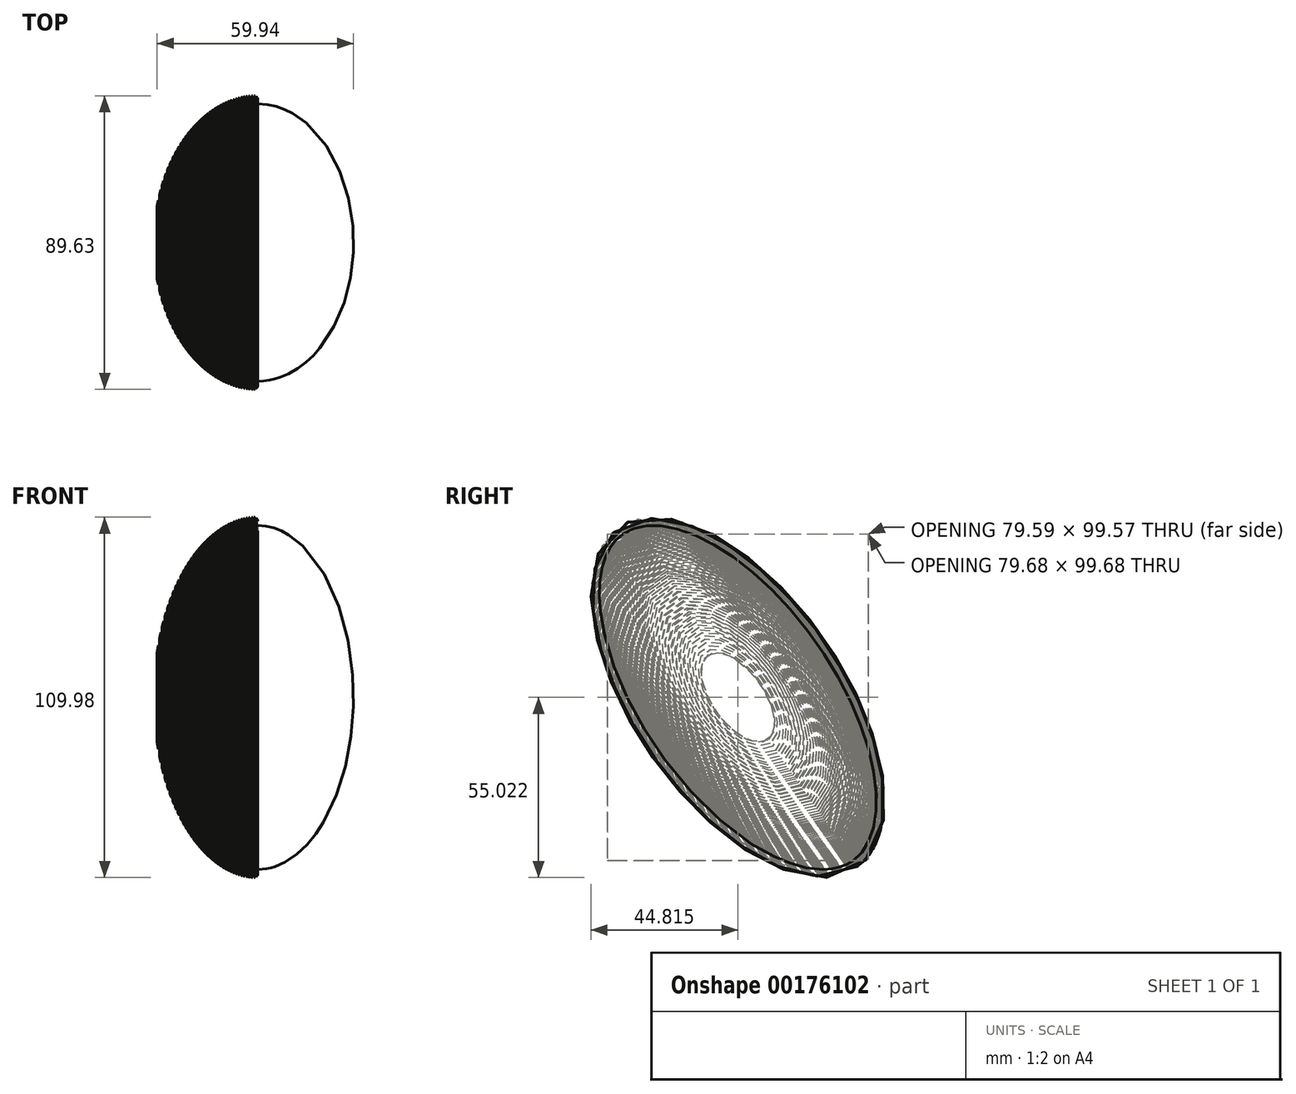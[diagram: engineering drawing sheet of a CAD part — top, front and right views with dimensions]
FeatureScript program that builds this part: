
annotation { "Feature Type Name" : "Feature", "Feature Type Description" : "" }
export const myFeature = defineFeature(function(context is Context, id is Id, definition is map)
    precondition{}
    {
        {
            var Q0;
            Q0=qCreatedBy(makeId("Right.planeOp"),FACE);
            var sketch = newSketch(context, id + "F0", { "sketchPlane" : qUnion([Q0])});
            skEllipse(sketch, "E0", {"center": v(0, 0) * mm, "majorRadius": 63.5 * mm, "minorRadius": 31.75 * mm, "majorAxis": v(-0.58, 0.82)});
            skLineSegment(sketch, "E1", {"start": v(0, 0) * mm, "end": v(-36.58, 51.9) * mm});
            skLineSegment(sketch, "E2", {"start": v(-36.58, 51.9) * mm, "end": v(36.58, -51.9) * mm});
            skSolve(sketch);
        }
        {
            var Q0;
            {var subQ0=sQuery(id+"F0.wireOp",EDGE,"E2");var subQ4=makeQuery(id+"F0.imprint","IMPRINT",VERTEX,{"derivedFrom":subQ0});Q0=makeQuery(id+"F0.imprint","IMPRINT",FACE,{"disambiguationData":[TD([[makeQuery(id+"F0.imprint","IMPRINT",EDGE,{"disambiguationData":[TD([[subQ4,1.0]])],"derivedFrom":subQ0}),-1.0]])]});}
            var Q1;
            Q1=sQuery(id+"F0.wireOp",EDGE,"E2");
            revolve(context, id + "F1", {"entities" : qUnion([Q0]), "axis" : qUnion([Q1]), "revolveType" : RevolveType.ONE_DIRECTION, "angle" : 180 * degree});
        }
        {
            var Q0;
            Q0=qCreatedBy(makeId("Right.planeOp"),FACE);
            cPlane(context, id + "F2", {"entities" : qUnion([Q0]), "cplaneType" : CPlaneType.OFFSET, "offset" : 30.73 * mm, "oppositeDirection" : true, "width" : 152.4 * mm, "height" : 152.4 * mm});
        }
        {
            var Q0;
            Q0=qCreatedBy(id+"F2.planeOp",FACE);
            var sketch = newSketch(context, id + "F3", { "sketchPlane" : qUnion([Q0])});
            skLineSegment(sketch, "E3.bottom", {"start": v(33.92, 43.72) * mm, "end": v(-38.1, 43.72) * mm});
            skLineSegment(sketch, "E3.top", {"start": v(33.92, -43.72) * mm, "end": v(-38.1, -43.72) * mm});
            skLineSegment(sketch, "E3.left", {"start": v(33.92, 43.72) * mm, "end": v(33.92, -43.72) * mm});
            skLineSegment(sketch, "E3.right", {"start": v(-38.1, 43.72) * mm, "end": v(-38.1, -43.72) * mm});
            skPoint(sketch, "E3.middle", {"position": v(-2.08, 0) * mm});
            skSolve(sketch);
        }
        {
            var Q0;
            Q0 = qSketchRegion(id + "F3", true);
            extrude(context, id + "F4", {"entities" : qUnion([Q0]), "operationType" : NewBodyOperationType.REMOVE, "oppositeDirection" : true, "depth" : 25.4 * mm});
        }
        {
            var Q0;
            Q0=makeQuery(id+"F1.opRevolve","CAP_FACE",FACE,{"disambiguationData":[OSD([sQuery(id+"F0.wireOp",EDGE,"E0"),sQuery(id+"F0.wireOp",EDGE,"E2")])],"isStart":false});
            shell(context, id + "F5", {"entities" : qUnion([Q0]), "thickness" : 2.54 * mm});
        }
        {
            var Q0;
            {var subQ0=sQuery(id+"F0.wireOp",EDGE,"E0");Q0=makeQuery(id+"F5.opShell","OFFSET_EDGE",EDGE,{"disambiguationData":[OSD([subQ0]),TDD([makeQuery(id+"F1.opRevolve","CAP_EDGE",EDGE,{"disambiguationData":[OSD([subQ0])],"isStart":true})])]});}
            var Q1;
            Q1=makeQuery(id+"F1.opRevolve","CAP_EDGE",EDGE,{"disambiguationData":[OSD([sQuery(id+"F0.wireOp",EDGE,"E0")])],"isStart":true});
            fillet(context, id + "F6", {"entities" : qUnion([Q0, Q1]), "radius" : 1.24 * mm, "tangentPropagation" : true, "allowEdgeOverflow" : false});
        }
        {
            var Q0;
            Q0=qCreatedBy(makeId("Right.planeOp"),FACE);
            cPlane(context, id + "F7", {"entities" : qUnion([Q0]), "cplaneType" : CPlaneType.OFFSET, "offset" : .4 * mm, "oppositeDirection" : true, "width" : 152.4 * mm, "height" : 152.4 * mm});
        }
        {
            var Q0;
            Q0=qCreatedBy(id+"F7.planeOp",FACE);
            cPlane(context, id + "F8", {"entities" : qUnion([Q0]), "cplaneType" : CPlaneType.OFFSET, "offset" : .8 * mm, "oppositeDirection" : true, "width" : 152.4 * mm, "height" : 152.4 * mm});
        }
        {
            var Q0;
            Q0=qCreatedBy(id+"F8.planeOp",FACE);
            cPlane(context, id + "F9", {"entities" : qUnion([Q0]), "cplaneType" : CPlaneType.OFFSET, "offset" : .8 * mm, "oppositeDirection" : true, "width" : 152.4 * mm, "height" : 152.4 * mm});
        }
        {
            var Q0;
            Q0=qCreatedBy(id+"F9.planeOp",FACE);
            cPlane(context, id + "F10", {"entities" : qUnion([Q0]), "cplaneType" : CPlaneType.OFFSET, "offset" : .8 * mm, "oppositeDirection" : true, "width" : 152.4 * mm, "height" : 152.4 * mm});
        }
        {
            var Q0;
            Q0=qCreatedBy(id+"F10.planeOp",FACE);
            cPlane(context, id + "F11", {"entities" : qUnion([Q0]), "cplaneType" : CPlaneType.OFFSET, "offset" : .8 * mm, "oppositeDirection" : true, "width" : 152.4 * mm, "height" : 152.4 * mm});
        }
        {
            var Q0;
            Q0=qCreatedBy(id+"F11.planeOp",FACE);
            cPlane(context, id + "F12", {"entities" : qUnion([Q0]), "cplaneType" : CPlaneType.OFFSET, "offset" : .8 * mm, "oppositeDirection" : true, "width" : 152.4 * mm, "height" : 152.4 * mm});
        }
        {
            var Q0;
            Q0=qCreatedBy(id+"F12.planeOp",FACE);
            cPlane(context, id + "F13", {"entities" : qUnion([Q0]), "cplaneType" : CPlaneType.OFFSET, "offset" : .8 * mm, "oppositeDirection" : true, "width" : 152.4 * mm, "height" : 152.4 * mm});
        }
        {
            var Q0;
            Q0=qCreatedBy(id+"F13.planeOp",FACE);
            cPlane(context, id + "F14", {"entities" : qUnion([Q0]), "cplaneType" : CPlaneType.OFFSET, "offset" : .8 * mm, "oppositeDirection" : true, "width" : 152.4 * mm, "height" : 152.4 * mm});
        }
        {
            var Q0;
            Q0=qCreatedBy(id+"F14.planeOp",FACE);
            cPlane(context, id + "F15", {"entities" : qUnion([Q0]), "cplaneType" : CPlaneType.OFFSET, "offset" : .8 * mm, "oppositeDirection" : true, "width" : 152.4 * mm, "height" : 152.4 * mm});
        }
        {
            var Q0;
            Q0=qCreatedBy(id+"F15.planeOp",FACE);
            cPlane(context, id + "F16", {"entities" : qUnion([Q0]), "cplaneType" : CPlaneType.OFFSET, "offset" : .8 * mm, "oppositeDirection" : true, "width" : 152.4 * mm, "height" : 152.4 * mm});
        }
        {
            var Q0;
            Q0=qCreatedBy(id+"F16.planeOp",FACE);
            cPlane(context, id + "F17", {"entities" : qUnion([Q0]), "cplaneType" : CPlaneType.OFFSET, "offset" : .8 * mm, "oppositeDirection" : true, "width" : 152.4 * mm, "height" : 152.4 * mm});
        }
        {
            var Q0;
            Q0=qCreatedBy(id+"F17.planeOp",FACE);
            cPlane(context, id + "F18", {"entities" : qUnion([Q0]), "cplaneType" : CPlaneType.OFFSET, "offset" : .8 * mm, "oppositeDirection" : true, "width" : 152.4 * mm, "height" : 152.4 * mm});
        }
        {
            var Q0;
            Q0=qCreatedBy(id+"F18.planeOp",FACE);
            cPlane(context, id + "F19", {"entities" : qUnion([Q0]), "cplaneType" : CPlaneType.OFFSET, "offset" : .8 * mm, "oppositeDirection" : true, "width" : 152.4 * mm, "height" : 152.4 * mm});
        }
        {
            var Q0;
            Q0=qCreatedBy(id+"F19.planeOp",FACE);
            cPlane(context, id + "F20", {"entities" : qUnion([Q0]), "cplaneType" : CPlaneType.OFFSET, "offset" : .8 * mm, "oppositeDirection" : true, "width" : 152.4 * mm, "height" : 152.4 * mm});
        }
        {
            var Q0;
            Q0=qCreatedBy(id+"F20.planeOp",FACE);
            cPlane(context, id + "F21", {"entities" : qUnion([Q0]), "cplaneType" : CPlaneType.OFFSET, "offset" : .8 * mm, "oppositeDirection" : true, "width" : 152.4 * mm, "height" : 152.4 * mm});
        }
        {
            var Q0;
            Q0=qCreatedBy(id+"F21.planeOp",FACE);
            cPlane(context, id + "F22", {"entities" : qUnion([Q0]), "cplaneType" : CPlaneType.OFFSET, "offset" : .8 * mm, "oppositeDirection" : true, "width" : 152.4 * mm, "height" : 152.4 * mm});
        }
        {
            var Q0;
            Q0=qCreatedBy(id+"F22.planeOp",FACE);
            cPlane(context, id + "F23", {"entities" : qUnion([Q0]), "cplaneType" : CPlaneType.OFFSET, "offset" : .8 * mm, "oppositeDirection" : true, "width" : 152.4 * mm, "height" : 152.4 * mm});
        }
        {
            var Q0;
            Q0=qCreatedBy(id+"F23.planeOp",FACE);
            cPlane(context, id + "F24", {"entities" : qUnion([Q0]), "cplaneType" : CPlaneType.OFFSET, "offset" : .8 * mm, "oppositeDirection" : true, "width" : 152.4 * mm, "height" : 152.4 * mm});
        }
        {
            var Q0;
            Q0=qCreatedBy(id+"F24.planeOp",FACE);
            cPlane(context, id + "F25", {"entities" : qUnion([Q0]), "cplaneType" : CPlaneType.OFFSET, "offset" : .8 * mm, "oppositeDirection" : true, "width" : 152.4 * mm, "height" : 152.4 * mm});
        }
        {
            var Q0;
            Q0=qCreatedBy(id+"F25.planeOp",FACE);
            cPlane(context, id + "F26", {"entities" : qUnion([Q0]), "cplaneType" : CPlaneType.OFFSET, "offset" : .8 * mm, "oppositeDirection" : true, "width" : 152.4 * mm, "height" : 152.4 * mm});
        }
        {
            var Q0;
            Q0=qCreatedBy(id+"F26.planeOp",FACE);
            cPlane(context, id + "F27", {"entities" : qUnion([Q0]), "cplaneType" : CPlaneType.OFFSET, "offset" : .8 * mm, "oppositeDirection" : true, "width" : 152.4 * mm, "height" : 152.4 * mm});
        }
        {
            var Q0;
            Q0=qCreatedBy(id+"F27.planeOp",FACE);
            cPlane(context, id + "F28", {"entities" : qUnion([Q0]), "cplaneType" : CPlaneType.OFFSET, "offset" : .8 * mm, "oppositeDirection" : true, "width" : 152.4 * mm, "height" : 152.4 * mm});
        }
        {
            var Q0;
            Q0=qCreatedBy(id+"F28.planeOp",FACE);
            cPlane(context, id + "F29", {"entities" : qUnion([Q0]), "cplaneType" : CPlaneType.OFFSET, "offset" : .8 * mm, "oppositeDirection" : true, "width" : 152.4 * mm, "height" : 152.4 * mm});
        }
        {
            var Q0;
            Q0=qCreatedBy(id+"F29.planeOp",FACE);
            cPlane(context, id + "F30", {"entities" : qUnion([Q0]), "cplaneType" : CPlaneType.OFFSET, "offset" : .8 * mm, "oppositeDirection" : true, "width" : 152.4 * mm, "height" : 152.4 * mm});
        }
        {
            var Q0;
            Q0=qCreatedBy(id+"F30.planeOp",FACE);
            cPlane(context, id + "F31", {"entities" : qUnion([Q0]), "cplaneType" : CPlaneType.OFFSET, "offset" : .8 * mm, "oppositeDirection" : true, "width" : 152.4 * mm, "height" : 152.4 * mm});
        }
        {
            var Q0;
            Q0=qCreatedBy(id+"F31.planeOp",FACE);
            cPlane(context, id + "F32", {"entities" : qUnion([Q0]), "cplaneType" : CPlaneType.OFFSET, "offset" : .8 * mm, "oppositeDirection" : true, "width" : 152.4 * mm, "height" : 152.4 * mm});
        }
        {
            var Q0;
            Q0=qCreatedBy(id+"F32.planeOp",FACE);
            cPlane(context, id + "F33", {"entities" : qUnion([Q0]), "cplaneType" : CPlaneType.OFFSET, "offset" : .8 * mm, "oppositeDirection" : true, "width" : 152.4 * mm, "height" : 152.4 * mm});
        }
        {
            var Q0;
            Q0=qCreatedBy(id+"F33.planeOp",FACE);
            cPlane(context, id + "F34", {"entities" : qUnion([Q0]), "cplaneType" : CPlaneType.OFFSET, "offset" : .8 * mm, "oppositeDirection" : true, "width" : 152.4 * mm, "height" : 152.4 * mm});
        }
        {
            var Q0;
            Q0=qCreatedBy(id+"F34.planeOp",FACE);
            cPlane(context, id + "F35", {"entities" : qUnion([Q0]), "cplaneType" : CPlaneType.OFFSET, "offset" : .8 * mm, "oppositeDirection" : true, "width" : 152.4 * mm, "height" : 152.4 * mm});
        }
        {
            var Q0;
            Q0=qCreatedBy(id+"F35.planeOp",FACE);
            cPlane(context, id + "F36", {"entities" : qUnion([Q0]), "cplaneType" : CPlaneType.OFFSET, "offset" : .8 * mm, "oppositeDirection" : true, "width" : 152.4 * mm, "height" : 152.4 * mm});
        }
        {
            var Q0;
            Q0=qCreatedBy(id+"F36.planeOp",FACE);
            cPlane(context, id + "F37", {"entities" : qUnion([Q0]), "cplaneType" : CPlaneType.OFFSET, "offset" : .8 * mm, "oppositeDirection" : true, "width" : 152.4 * mm, "height" : 152.4 * mm});
        }
        {
            var Q0;
            Q0=qCreatedBy(id+"F37.planeOp",FACE);
            cPlane(context, id + "F38", {"entities" : qUnion([Q0]), "cplaneType" : CPlaneType.OFFSET, "offset" : .8 * mm, "oppositeDirection" : true, "width" : 152.4 * mm, "height" : 152.4 * mm});
        }
        {
            var Q0;
            Q0=qCreatedBy(id+"F38.planeOp",FACE);
            cPlane(context, id + "F39", {"entities" : qUnion([Q0]), "cplaneType" : CPlaneType.OFFSET, "offset" : .8 * mm, "oppositeDirection" : true, "width" : 152.4 * mm, "height" : 152.4 * mm});
        }
        {
            var Q0;
            Q0=qCreatedBy(id+"F39.planeOp",FACE);
            cPlane(context, id + "F40", {"entities" : qUnion([Q0]), "cplaneType" : CPlaneType.OFFSET, "offset" : .8 * mm, "oppositeDirection" : true, "width" : 152.4 * mm, "height" : 152.4 * mm});
        }
        {
            var Q0;
            Q0=qCreatedBy(id+"F40.planeOp",FACE);
            cPlane(context, id + "F41", {"entities" : qUnion([Q0]), "cplaneType" : CPlaneType.OFFSET, "offset" : .8 * mm, "oppositeDirection" : true, "width" : 152.4 * mm, "height" : 152.4 * mm});
        }
        {
            var Q0;
            Q0=qCreatedBy(id+"F41.planeOp",FACE);
            cPlane(context, id + "F42", {"entities" : qUnion([Q0]), "cplaneType" : CPlaneType.OFFSET, "offset" : .8 * mm, "oppositeDirection" : true, "width" : 152.4 * mm, "height" : 152.4 * mm});
        }
        {
            var Q0;
            Q0=qCreatedBy(id+"F42.planeOp",FACE);
            cPlane(context, id + "F43", {"entities" : qUnion([Q0]), "cplaneType" : CPlaneType.OFFSET, "offset" : .8 * mm, "oppositeDirection" : true, "width" : 152.4 * mm, "height" : 152.4 * mm});
        }
        {
            var Q0;
            Q0=qCreatedBy(id+"F43.planeOp",FACE);
            cPlane(context, id + "F44", {"entities" : qUnion([Q0]), "cplaneType" : CPlaneType.OFFSET, "offset" : .8 * mm, "oppositeDirection" : true, "width" : 152.4 * mm, "height" : 152.4 * mm});
        }
        {
            var Q0;
            Q0=qCreatedBy(id+"F7.planeOp",FACE);
            var sketch = newSketch(context, id + "F45", { "sketchPlane" : qUnion([Q0])});
            skLineSegment(sketch, "E4.bottom", {"start": v(-49.25, 57.03) * mm, "end": v(49.25, 57.03) * mm});
            skLineSegment(sketch, "E4.top", {"start": v(-49.25, -57.03) * mm, "end": v(49.25, -57.03) * mm});
            skLineSegment(sketch, "E4.left", {"start": v(-49.25, 57.03) * mm, "end": v(-49.25, -57.03) * mm});
            skLineSegment(sketch, "E4.right", {"start": v(49.25, 57.03) * mm, "end": v(49.25, -57.03) * mm});
            skPoint(sketch, "E4.middle", {"position": v(0, 0) * mm});
            skSolve(sketch);
        }
        {
            var Q0;
            Q0 = qSketchRegion(id + "F45", true);
            extrude(context, id + "F46", {"entities" : qUnion([Q0]), "operationType" : NewBodyOperationType.REMOVE, "oppositeDirection" : true, "depth" : .4 * mm});
        }
        {
            var Q0;
            Q0=qCreatedBy(id+"F8.planeOp",FACE);
            var sketch = newSketch(context, id + "F47", { "sketchPlane" : qUnion([Q0])});
            skLineSegment(sketch, "E5.bottom", {"start": v(53.57, 63.62) * mm, "end": v(-53.57, 63.62) * mm});
            skLineSegment(sketch, "E5.top", {"start": v(53.57, -63.62) * mm, "end": v(-53.57, -63.62) * mm});
            skLineSegment(sketch, "E5.left", {"start": v(53.57, 63.62) * mm, "end": v(53.57, -63.62) * mm});
            skLineSegment(sketch, "E5.right", {"start": v(-53.57, 63.62) * mm, "end": v(-53.57, -63.62) * mm});
            skPoint(sketch, "E5.middle", {"position": v(0, 0) * mm});
            skSolve(sketch);
        }
        {
            var Q0;
            Q0 = qSketchRegion(id + "F47", true);
            extrude(context, id + "F48", {"entities" : qUnion([Q0]), "operationType" : NewBodyOperationType.REMOVE, "oppositeDirection" : true, "depth" : .4 * mm});
        }
        {
            var Q0;
            Q0=qCreatedBy(id+"F9.planeOp",FACE);
            var sketch = newSketch(context, id + "F49", { "sketchPlane" : qUnion([Q0])});
            skLineSegment(sketch, "E6.bottom", {"start": v(-59.34, 63.85) * mm, "end": v(59.34, 63.85) * mm});
            skLineSegment(sketch, "E6.top", {"start": v(-59.34, -63.85) * mm, "end": v(59.34, -63.85) * mm});
            skLineSegment(sketch, "E6.left", {"start": v(-59.34, 63.85) * mm, "end": v(-59.34, -63.85) * mm});
            skLineSegment(sketch, "E6.right", {"start": v(59.34, 63.85) * mm, "end": v(59.34, -63.85) * mm});
            skPoint(sketch, "E6.middle", {"position": v(0, 0) * mm});
            skSolve(sketch);
        }
        {
            var Q0;
            Q0 = qSketchRegion(id + "F49", true);
            extrude(context, id + "F50", {"entities" : qUnion([Q0]), "operationType" : NewBodyOperationType.REMOVE, "oppositeDirection" : true, "depth" : .4 * mm});
        }
        {
            var Q0;
            Q0=qCreatedBy(id+"F10.planeOp",FACE);
            var sketch = newSketch(context, id + "F51", { "sketchPlane" : qUnion([Q0])});
            skLineSegment(sketch, "E7.bottom", {"start": v(-54.53, 72.46) * mm, "end": v(54.53, 72.46) * mm});
            skLineSegment(sketch, "E7.top", {"start": v(-54.53, -72.46) * mm, "end": v(54.53, -72.46) * mm});
            skLineSegment(sketch, "E7.left", {"start": v(-54.53, 72.46) * mm, "end": v(-54.53, -72.46) * mm});
            skLineSegment(sketch, "E7.right", {"start": v(54.53, 72.46) * mm, "end": v(54.53, -72.46) * mm});
            skPoint(sketch, "E7.middle", {"position": v(0, 0) * mm});
            skSolve(sketch);
        }
        {
            var Q0;
            Q0 = qSketchRegion(id + "F51", true);
            extrude(context, id + "F52", {"entities" : qUnion([Q0]), "operationType" : NewBodyOperationType.REMOVE, "oppositeDirection" : true, "depth" : .4 * mm});
        }
        {
            var Q0;
            Q0=qCreatedBy(id+"F11.planeOp",FACE);
            var sketch = newSketch(context, id + "F53", { "sketchPlane" : qUnion([Q0])});
            skLineSegment(sketch, "E8.bottom", {"start": v(-58.86, 71.77) * mm, "end": v(71.33, 71.77) * mm});
            skLineSegment(sketch, "E8.top", {"start": v(-58.86, -71.77) * mm, "end": v(71.33, -71.77) * mm});
            skLineSegment(sketch, "E8.left", {"start": v(-58.86, 71.77) * mm, "end": v(-58.86, -71.77) * mm});
            skLineSegment(sketch, "E8.right", {"start": v(71.33, 71.77) * mm, "end": v(71.33, -71.77) * mm});
            skPoint(sketch, "E8.middle", {"position": v(6.24, 0) * mm});
            skSolve(sketch);
        }
        {
            var Q0;
            Q0 = qSketchRegion(id + "F53", true);
            extrude(context, id + "F54", {"entities" : qUnion([Q0]), "operationType" : NewBodyOperationType.REMOVE, "oppositeDirection" : true, "depth" : .4 * mm});
        }
        {
            var Q0;
            Q0=qCreatedBy(id+"F12.planeOp",FACE);
            var sketch = newSketch(context, id + "F55", { "sketchPlane" : qUnion([Q0])});
            skLineSegment(sketch, "E9.bottom", {"start": v(65.58, 62.46) * mm, "end": v(-65.58, 62.46) * mm});
            skLineSegment(sketch, "E9.top", {"start": v(65.58, -62.46) * mm, "end": v(-65.58, -62.46) * mm});
            skLineSegment(sketch, "E9.left", {"start": v(65.58, 62.46) * mm, "end": v(65.58, -62.46) * mm});
            skLineSegment(sketch, "E9.right", {"start": v(-65.58, 62.46) * mm, "end": v(-65.58, -62.46) * mm});
            skPoint(sketch, "E9.middle", {"position": v(0, 0) * mm});
            skSolve(sketch);
        }
        {
            var Q0;
            Q0=qCreatedBy(id+"F13.planeOp",FACE);
            var sketch = newSketch(context, id + "F56", { "sketchPlane" : qUnion([Q0])});
            skLineSegment(sketch, "E10.bottom", {"start": v(67.66, 61.77) * mm, "end": v(-67.66, 61.77) * mm});
            skLineSegment(sketch, "E10.top", {"start": v(67.66, -61.77) * mm, "end": v(-67.66, -61.77) * mm});
            skLineSegment(sketch, "E10.left", {"start": v(67.66, 61.77) * mm, "end": v(67.66, -61.77) * mm});
            skLineSegment(sketch, "E10.right", {"start": v(-67.66, 61.77) * mm, "end": v(-67.66, -61.77) * mm});
            skPoint(sketch, "E10.middle", {"position": v(0, 0) * mm});
            skSolve(sketch);
        }
        {
            var Q0;
            Q0=qCreatedBy(id+"F14.planeOp",FACE);
            var sketch = newSketch(context, id + "F57", { "sketchPlane" : qUnion([Q0])});
            skLineSegment(sketch, "E11.bottom", {"start": v(70.2, 68.7) * mm, "end": v(-70.2, 68.7) * mm});
            skLineSegment(sketch, "E11.top", {"start": v(70.2, -68.7) * mm, "end": v(-70.2, -68.7) * mm});
            skLineSegment(sketch, "E11.left", {"start": v(70.2, 68.7) * mm, "end": v(70.2, -68.7) * mm});
            skLineSegment(sketch, "E11.right", {"start": v(-70.2, 68.7) * mm, "end": v(-70.2, -68.7) * mm});
            skPoint(sketch, "E11.middle", {"position": v(0, 0) * mm});
            skSolve(sketch);
        }
        {
            var Q0;
            Q0=qCreatedBy(id+"F15.planeOp",FACE);
            var sketch = newSketch(context, id + "F58", { "sketchPlane" : qUnion([Q0])});
            skLineSegment(sketch, "E12.bottom", {"start": v(66.27, 65) * mm, "end": v(-66.27, 65) * mm});
            skLineSegment(sketch, "E12.top", {"start": v(66.27, -65) * mm, "end": v(-66.27, -65) * mm});
            skLineSegment(sketch, "E12.left", {"start": v(66.27, 65) * mm, "end": v(66.27, -65) * mm});
            skLineSegment(sketch, "E12.right", {"start": v(-66.27, 65) * mm, "end": v(-66.27, -65) * mm});
            skPoint(sketch, "E12.middle", {"position": v(0, 0) * mm});
            skSolve(sketch);
        }
        {
            var Q0;
            Q0=qCreatedBy(id+"F16.planeOp",FACE);
            var sketch = newSketch(context, id + "F59", { "sketchPlane" : qUnion([Q0])});
            skLineSegment(sketch, "E13.bottom", {"start": v(68.35, 68) * mm, "end": v(-68.35, 68) * mm});
            skLineSegment(sketch, "E13.top", {"start": v(68.35, -68) * mm, "end": v(-68.35, -68) * mm});
            skLineSegment(sketch, "E13.left", {"start": v(68.35, 68) * mm, "end": v(68.35, -68) * mm});
            skLineSegment(sketch, "E13.right", {"start": v(-68.35, 68) * mm, "end": v(-68.35, -68) * mm});
            skPoint(sketch, "E13.middle", {"position": v(0, 0) * mm});
            skSolve(sketch);
        }
        {
            var Q0;
            Q0=qCreatedBy(id+"F17.planeOp",FACE);
            var sketch = newSketch(context, id + "F60", { "sketchPlane" : qUnion([Q0])});
            skLineSegment(sketch, "E14.bottom", {"start": v(68.35, 68.46) * mm, "end": v(-68.35, 68.46) * mm});
            skLineSegment(sketch, "E14.top", {"start": v(68.35, -68.46) * mm, "end": v(-68.35, -68.46) * mm});
            skLineSegment(sketch, "E14.left", {"start": v(68.35, 68.46) * mm, "end": v(68.35, -68.46) * mm});
            skLineSegment(sketch, "E14.right", {"start": v(-68.35, 68.46) * mm, "end": v(-68.35, -68.46) * mm});
            skPoint(sketch, "E14.middle", {"position": v(0, 0) * mm});
            skSolve(sketch);
        }
        {
            var Q0;
            Q0=qCreatedBy(id+"F18.planeOp",FACE);
            var sketch = newSketch(context, id + "F61", { "sketchPlane" : qUnion([Q0])});
            skLineSegment(sketch, "E15.bottom", {"start": v(69.27, 68.46) * mm, "end": v(-69.27, 68.46) * mm});
            skLineSegment(sketch, "E15.top", {"start": v(69.27, -68.46) * mm, "end": v(-69.27, -68.46) * mm});
            skLineSegment(sketch, "E15.left", {"start": v(69.27, 68.46) * mm, "end": v(69.27, -68.46) * mm});
            skLineSegment(sketch, "E15.right", {"start": v(-69.27, 68.46) * mm, "end": v(-69.27, -68.46) * mm});
            skPoint(sketch, "E15.middle", {"position": v(0, 0) * mm});
            skSolve(sketch);
        }
        {
            var Q0;
            Q0=qCreatedBy(id+"F19.planeOp",FACE);
            var sketch = newSketch(context, id + "F62", { "sketchPlane" : qUnion([Q0])});
            skLineSegment(sketch, "E16.bottom", {"start": v(69.73, 68) * mm, "end": v(-69.73, 68) * mm});
            skLineSegment(sketch, "E16.top", {"start": v(69.73, -68) * mm, "end": v(-69.73, -68) * mm});
            skLineSegment(sketch, "E16.left", {"start": v(69.73, 68) * mm, "end": v(69.73, -68) * mm});
            skLineSegment(sketch, "E16.right", {"start": v(-69.73, 68) * mm, "end": v(-69.73, -68) * mm});
            skPoint(sketch, "E16.middle", {"position": v(0, 0) * mm});
            skSolve(sketch);
        }
        {
            var Q0;
            Q0=qCreatedBy(id+"F20.planeOp",FACE);
            var sketch = newSketch(context, id + "F63", { "sketchPlane" : qUnion([Q0])});
            skLineSegment(sketch, "E17.bottom", {"start": v(70.89, 67.3) * mm, "end": v(-70.89, 67.3) * mm});
            skLineSegment(sketch, "E17.top", {"start": v(70.89, -67.3) * mm, "end": v(-70.89, -67.3) * mm});
            skLineSegment(sketch, "E17.left", {"start": v(70.89, 67.3) * mm, "end": v(70.89, -67.3) * mm});
            skLineSegment(sketch, "E17.right", {"start": v(-70.89, 67.3) * mm, "end": v(-70.89, -67.3) * mm});
            skPoint(sketch, "E17.middle", {"position": v(0, 0) * mm});
            skSolve(sketch);
        }
        {
            var Q0;
            Q0=qCreatedBy(id+"F21.planeOp",FACE);
            var sketch = newSketch(context, id + "F64", { "sketchPlane" : qUnion([Q0])});
            skLineSegment(sketch, "E18.bottom", {"start": v(69.97, 66.62) * mm, "end": v(-69.97, 66.62) * mm});
            skLineSegment(sketch, "E18.top", {"start": v(69.97, -66.62) * mm, "end": v(-69.97, -66.62) * mm});
            skLineSegment(sketch, "E18.left", {"start": v(69.97, 66.62) * mm, "end": v(69.97, -66.62) * mm});
            skLineSegment(sketch, "E18.right", {"start": v(-69.97, 66.62) * mm, "end": v(-69.97, -66.62) * mm});
            skPoint(sketch, "E18.middle", {"position": v(0, 0) * mm});
            skSolve(sketch);
        }
        {
            var Q0;
            Q0=qCreatedBy(id+"F22.planeOp",FACE);
            var sketch = newSketch(context, id + "F65", { "sketchPlane" : qUnion([Q0])});
            skLineSegment(sketch, "E19.bottom", {"start": v(70.2, 67.3) * mm, "end": v(-70.2, 67.3) * mm});
            skLineSegment(sketch, "E19.top", {"start": v(70.2, -67.3) * mm, "end": v(-70.2, -67.3) * mm});
            skLineSegment(sketch, "E19.left", {"start": v(70.2, 67.3) * mm, "end": v(70.2, -67.3) * mm});
            skLineSegment(sketch, "E19.right", {"start": v(-70.2, 67.3) * mm, "end": v(-70.2, -67.3) * mm});
            skPoint(sketch, "E19.middle", {"position": v(0, 0) * mm});
            skSolve(sketch);
        }
        {
            var Q0;
            Q0=qCreatedBy(id+"F23.planeOp",FACE);
            var sketch = newSketch(context, id + "F66", { "sketchPlane" : qUnion([Q0])});
            skLineSegment(sketch, "E20.bottom", {"start": v(-68.35, 66.85) * mm, "end": v(68.35, 66.85) * mm});
            skLineSegment(sketch, "E20.top", {"start": v(-68.35, -66.85) * mm, "end": v(68.35, -66.85) * mm});
            skLineSegment(sketch, "E20.left", {"start": v(-68.35, 66.85) * mm, "end": v(-68.35, -66.85) * mm});
            skLineSegment(sketch, "E20.right", {"start": v(68.35, 66.85) * mm, "end": v(68.35, -66.85) * mm});
            skPoint(sketch, "E20.middle", {"position": v(0, 0) * mm});
            skSolve(sketch);
        }
        {
            var Q0;
            Q0=qCreatedBy(id+"F24.planeOp",FACE);
            var sketch = newSketch(context, id + "F67", { "sketchPlane" : qUnion([Q0])});
            skLineSegment(sketch, "E21.bottom", {"start": v(-68.12, 65.23) * mm, "end": v(68.12, 65.23) * mm});
            skLineSegment(sketch, "E21.top", {"start": v(-68.12, -65.23) * mm, "end": v(68.12, -65.23) * mm});
            skLineSegment(sketch, "E21.left", {"start": v(-68.12, 65.23) * mm, "end": v(-68.12, -65.23) * mm});
            skLineSegment(sketch, "E21.right", {"start": v(68.12, 65.23) * mm, "end": v(68.12, -65.23) * mm});
            skPoint(sketch, "E21.middle", {"position": v(0, 0) * mm});
            skSolve(sketch);
        }
        {
            var Q0;
            Q0=qCreatedBy(id+"F25.planeOp",FACE);
            var sketch = newSketch(context, id + "F68", { "sketchPlane" : qUnion([Q0])});
            skLineSegment(sketch, "E22.bottom", {"start": v(-69.97, 67.08) * mm, "end": v(69.97, 67.08) * mm});
            skLineSegment(sketch, "E22.top", {"start": v(-69.97, -67.08) * mm, "end": v(69.97, -67.08) * mm});
            skLineSegment(sketch, "E22.left", {"start": v(-69.97, 67.08) * mm, "end": v(-69.97, -67.08) * mm});
            skLineSegment(sketch, "E22.right", {"start": v(69.97, 67.08) * mm, "end": v(69.97, -67.08) * mm});
            skPoint(sketch, "E22.middle", {"position": v(0, 0) * mm});
            skSolve(sketch);
        }
        {
            var Q0;
            Q0=qCreatedBy(id+"F26.planeOp",FACE);
            var sketch = newSketch(context, id + "F69", { "sketchPlane" : qUnion([Q0])});
            skLineSegment(sketch, "E23.bottom", {"start": v(-69.27, 66.85) * mm, "end": v(69.27, 66.85) * mm});
            skLineSegment(sketch, "E23.top", {"start": v(-69.27, -66.85) * mm, "end": v(69.27, -66.85) * mm});
            skLineSegment(sketch, "E23.left", {"start": v(-69.27, 66.85) * mm, "end": v(-69.27, -66.85) * mm});
            skLineSegment(sketch, "E23.right", {"start": v(69.27, 66.85) * mm, "end": v(69.27, -66.85) * mm});
            skPoint(sketch, "E23.middle", {"position": v(0, 0) * mm});
            skSolve(sketch);
        }
        {
            var Q0;
            Q0=qCreatedBy(id+"F27.planeOp",FACE);
            var sketch = newSketch(context, id + "F70", { "sketchPlane" : qUnion([Q0])});
            skLineSegment(sketch, "E24.bottom", {"start": v(-69.5, 66.62) * mm, "end": v(69.5, 66.62) * mm});
            skLineSegment(sketch, "E24.top", {"start": v(-69.5, -66.62) * mm, "end": v(69.5, -66.62) * mm});
            skLineSegment(sketch, "E24.left", {"start": v(-69.5, 66.62) * mm, "end": v(-69.5, -66.62) * mm});
            skLineSegment(sketch, "E24.right", {"start": v(69.5, 66.62) * mm, "end": v(69.5, -66.62) * mm});
            skPoint(sketch, "E24.middle", {"position": v(0, 0) * mm});
            skSolve(sketch);
        }
        {
            var Q0;
            Q0 = qSketchRegion(id + "F70", true);
            var Q1;
            Q1 = qSketchRegion(id + "F69", true);
            var Q2;
            Q2 = qSketchRegion(id + "F68", true);
            var Q3;
            Q3 = qSketchRegion(id + "F67", true);
            var Q4;
            Q4 = qSketchRegion(id + "F66", true);
            var Q5;
            Q5 = qSketchRegion(id + "F65", true);
            var Q6;
            Q6 = qSketchRegion(id + "F64", true);
            var Q7;
            Q7 = qSketchRegion(id + "F63", true);
            var Q8;
            Q8 = qSketchRegion(id + "F62", true);
            var Q9;
            Q9 = qSketchRegion(id + "F61", true);
            var Q10;
            Q10 = qSketchRegion(id + "F60", true);
            var Q11;
            Q11 = qSketchRegion(id + "F59", true);
            var Q12;
            Q12 = qSketchRegion(id + "F58", true);
            var Q13;
            Q13 = qSketchRegion(id + "F57", true);
            var Q14;
            Q14 = qSketchRegion(id + "F56", true);
            var Q15;
            Q15 = qSketchRegion(id + "F55", true);
            extrude(context, id + "F71", {"entities" : qUnion([Q0, Q1, Q2, Q3, Q4, Q5, Q6, Q7, Q8, Q9, Q10, Q11, Q12, Q13, Q14, Q15]), "operationType" : NewBodyOperationType.REMOVE, "oppositeDirection" : true, "depth" : .4 * mm});
        }
        {
            var Q0;
            Q0=qCreatedBy(id+"F28.planeOp",FACE);
            var sketch = newSketch(context, id + "F72", { "sketchPlane" : qUnion([Q0])});
            skLineSegment(sketch, "E25.bottom", {"start": v(-62.11, 65.46) * mm, "end": v(62.11, 65.46) * mm});
            skLineSegment(sketch, "E25.top", {"start": v(-62.11, -65.46) * mm, "end": v(62.11, -65.46) * mm});
            skLineSegment(sketch, "E25.left", {"start": v(-62.11, 65.46) * mm, "end": v(-62.11, -65.46) * mm});
            skLineSegment(sketch, "E25.right", {"start": v(62.11, 65.46) * mm, "end": v(62.11, -65.46) * mm});
            skPoint(sketch, "E25.middle", {"position": v(0, 0) * mm});
            skSolve(sketch);
        }
        {
            var Q0;
            Q0=qCreatedBy(id+"F29.planeOp",FACE);
            var sketch = newSketch(context, id + "F73", { "sketchPlane" : qUnion([Q0])});
            skLineSegment(sketch, "E26.bottom", {"start": v(-61.42, 65.23) * mm, "end": v(61.42, 65.23) * mm});
            skLineSegment(sketch, "E26.top", {"start": v(-61.42, -65.23) * mm, "end": v(61.42, -65.23) * mm});
            skLineSegment(sketch, "E26.left", {"start": v(-61.42, 65.23) * mm, "end": v(-61.42, -65.23) * mm});
            skLineSegment(sketch, "E26.right", {"start": v(61.42, 65.23) * mm, "end": v(61.42, -65.23) * mm});
            skPoint(sketch, "E26.middle", {"position": v(0, 0) * mm});
            skSolve(sketch);
        }
        {
            var Q0;
            Q0=qCreatedBy(id+"F30.planeOp",FACE);
            var sketch = newSketch(context, id + "F74", { "sketchPlane" : qUnion([Q0])});
            skLineSegment(sketch, "E27.bottom", {"start": v(-62.8, 65.23) * mm, "end": v(62.8, 65.23) * mm});
            skLineSegment(sketch, "E27.top", {"start": v(-62.8, -65.23) * mm, "end": v(62.8, -65.23) * mm});
            skLineSegment(sketch, "E27.left", {"start": v(-62.8, 65.23) * mm, "end": v(-62.8, -65.23) * mm});
            skLineSegment(sketch, "E27.right", {"start": v(62.8, 65.23) * mm, "end": v(62.8, -65.23) * mm});
            skPoint(sketch, "E27.middle", {"position": v(0, 0) * mm});
            skSolve(sketch);
        }
        {
            var Q0;
            Q0=qCreatedBy(id+"F31.planeOp",FACE);
            var sketch = newSketch(context, id + "F75", { "sketchPlane" : qUnion([Q0])});
            skLineSegment(sketch, "E28.bottom", {"start": v(-62.58, 64.54) * mm, "end": v(62.58, 64.54) * mm});
            skLineSegment(sketch, "E28.top", {"start": v(-62.58, -64.54) * mm, "end": v(62.58, -64.54) * mm});
            skLineSegment(sketch, "E28.left", {"start": v(-62.58, 64.54) * mm, "end": v(-62.58, -64.54) * mm});
            skLineSegment(sketch, "E28.right", {"start": v(62.58, 64.54) * mm, "end": v(62.58, -64.54) * mm});
            skPoint(sketch, "E28.middle", {"position": v(0, 0) * mm});
            skSolve(sketch);
        }
        {
            var Q0;
            Q0=qCreatedBy(id+"F32.planeOp",FACE);
            var sketch = newSketch(context, id + "F76", { "sketchPlane" : qUnion([Q0])});
            skLineSegment(sketch, "E29.bottom", {"start": v(-63.96, 65) * mm, "end": v(63.96, 65) * mm});
            skLineSegment(sketch, "E29.top", {"start": v(-63.96, -65) * mm, "end": v(63.96, -65) * mm});
            skLineSegment(sketch, "E29.left", {"start": v(-63.96, 65) * mm, "end": v(-63.96, -65) * mm});
            skLineSegment(sketch, "E29.right", {"start": v(63.96, 65) * mm, "end": v(63.96, -65) * mm});
            skPoint(sketch, "E29.middle", {"position": v(0, 0) * mm});
            skSolve(sketch);
        }
        {
            var Q0;
            Q0 = qSketchRegion(id + "F73", true);
            var Q1;
            Q1 = qSketchRegion(id + "F72", true);
            var Q2;
            Q2 = qSketchRegion(id + "F74", true);
            var Q3;
            Q3 = qSketchRegion(id + "F75", true);
            var Q4;
            Q4 = qSketchRegion(id + "F76", true);
            extrude(context, id + "F77", {"entities" : qUnion([Q0, Q1, Q2, Q3, Q4]), "operationType" : NewBodyOperationType.REMOVE, "oppositeDirection" : true, "depth" : .4 * mm});
        }
        {
            var Q0;
            Q0=qCreatedBy(id+"F33.planeOp",FACE);
            var sketch = newSketch(context, id + "F78", { "sketchPlane" : qUnion([Q0])});
            skLineSegment(sketch, "E30.bottom", {"start": v(67.11, 60.49) * mm, "end": v(-67.11, 60.49) * mm});
            skLineSegment(sketch, "E30.top", {"start": v(67.11, -60.49) * mm, "end": v(-67.11, -60.49) * mm});
            skLineSegment(sketch, "E30.left", {"start": v(67.11, 60.49) * mm, "end": v(67.11, -60.49) * mm});
            skLineSegment(sketch, "E30.right", {"start": v(-67.11, 60.49) * mm, "end": v(-67.11, -60.49) * mm});
            skPoint(sketch, "E30.middle", {"position": v(0, 0) * mm});
            skSolve(sketch);
        }
        {
            var Q0;
            Q0=qCreatedBy(id+"F34.planeOp",FACE);
            var sketch = newSketch(context, id + "F79", { "sketchPlane" : qUnion([Q0])});
            skLineSegment(sketch, "E31.bottom", {"start": v(66.92, 59.71) * mm, "end": v(-66.92, 59.71) * mm});
            skLineSegment(sketch, "E31.top", {"start": v(66.92, -59.71) * mm, "end": v(-66.92, -59.71) * mm});
            skLineSegment(sketch, "E31.left", {"start": v(66.92, 59.71) * mm, "end": v(66.92, -59.71) * mm});
            skLineSegment(sketch, "E31.right", {"start": v(-66.92, 59.71) * mm, "end": v(-66.92, -59.71) * mm});
            skPoint(sketch, "E31.middle", {"position": v(0, 0) * mm});
            skSolve(sketch);
        }
        {
            var Q0;
            Q0=qCreatedBy(id+"F35.planeOp",FACE);
            var sketch = newSketch(context, id + "F80", { "sketchPlane" : qUnion([Q0])});
            skLineSegment(sketch, "E32.bottom", {"start": v(66.72, 59.32) * mm, "end": v(-66.72, 59.32) * mm});
            skLineSegment(sketch, "E32.top", {"start": v(66.72, -59.32) * mm, "end": v(-66.72, -59.32) * mm});
            skLineSegment(sketch, "E32.left", {"start": v(66.72, 59.32) * mm, "end": v(66.72, -59.32) * mm});
            skLineSegment(sketch, "E32.right", {"start": v(-66.72, 59.32) * mm, "end": v(-66.72, -59.32) * mm});
            skPoint(sketch, "E32.middle", {"position": v(0, 0) * mm});
            skSolve(sketch);
        }
        {
            var Q0;
            Q0=qCreatedBy(id+"F36.planeOp",FACE);
            var sketch = newSketch(context, id + "F81", { "sketchPlane" : qUnion([Q0])});
            skLineSegment(sketch, "E33.bottom", {"start": v(67.11, 60.3) * mm, "end": v(-67.11, 60.3) * mm});
            skLineSegment(sketch, "E33.top", {"start": v(67.11, -60.3) * mm, "end": v(-67.11, -60.3) * mm});
            skLineSegment(sketch, "E33.left", {"start": v(67.11, 60.3) * mm, "end": v(67.11, -60.3) * mm});
            skLineSegment(sketch, "E33.right", {"start": v(-67.11, 60.3) * mm, "end": v(-67.11, -60.3) * mm});
            skPoint(sketch, "E33.middle", {"position": v(0, 0) * mm});
            skSolve(sketch);
        }
        {
            var Q0;
            Q0=qCreatedBy(id+"F37.planeOp",FACE);
            var sketch = newSketch(context, id + "F82", { "sketchPlane" : qUnion([Q0])});
            skLineSegment(sketch, "E34.bottom", {"start": v(66.72, 59.9) * mm, "end": v(-66.72, 59.9) * mm});
            skLineSegment(sketch, "E34.top", {"start": v(66.72, -59.9) * mm, "end": v(-66.72, -59.9) * mm});
            skLineSegment(sketch, "E34.left", {"start": v(66.72, 59.9) * mm, "end": v(66.72, -59.9) * mm});
            skLineSegment(sketch, "E34.right", {"start": v(-66.72, 59.9) * mm, "end": v(-66.72, -59.9) * mm});
            skPoint(sketch, "E34.middle", {"position": v(0, 0) * mm});
            skSolve(sketch);
        }
        {
            var Q0;
            Q0=qCreatedBy(id+"F38.planeOp",FACE);
            var sketch = newSketch(context, id + "F83", { "sketchPlane" : qUnion([Q0])});
            skLineSegment(sketch, "E35.bottom", {"start": v(66.72, 58.74) * mm, "end": v(-66.72, 58.74) * mm});
            skLineSegment(sketch, "E35.top", {"start": v(66.72, -58.74) * mm, "end": v(-66.72, -58.74) * mm});
            skLineSegment(sketch, "E35.left", {"start": v(66.72, 58.74) * mm, "end": v(66.72, -58.74) * mm});
            skLineSegment(sketch, "E35.right", {"start": v(-66.72, 58.74) * mm, "end": v(-66.72, -58.74) * mm});
            skPoint(sketch, "E35.middle", {"position": v(0, 0) * mm});
            skSolve(sketch);
        }
        {
            var Q0;
            Q0=qCreatedBy(id+"F39.planeOp",FACE);
            var sketch = newSketch(context, id + "F84", { "sketchPlane" : qUnion([Q0])});
            skLineSegment(sketch, "E36.bottom", {"start": v(66.92, 58.55) * mm, "end": v(-66.92, 58.55) * mm});
            skLineSegment(sketch, "E36.top", {"start": v(66.92, -58.55) * mm, "end": v(-66.92, -58.55) * mm});
            skLineSegment(sketch, "E36.left", {"start": v(66.92, 58.55) * mm, "end": v(66.92, -58.55) * mm});
            skLineSegment(sketch, "E36.right", {"start": v(-66.92, 58.55) * mm, "end": v(-66.92, -58.55) * mm});
            skPoint(sketch, "E36.middle", {"position": v(0, 0) * mm});
            skSolve(sketch);
        }
        {
            var Q0;
            Q0=qCreatedBy(id+"F40.planeOp",FACE);
            var sketch = newSketch(context, id + "F85", { "sketchPlane" : qUnion([Q0])});
            skLineSegment(sketch, "E37.bottom", {"start": v(66.33, 58.93) * mm, "end": v(-66.33, 58.93) * mm});
            skLineSegment(sketch, "E37.top", {"start": v(66.33, -58.93) * mm, "end": v(-66.33, -58.93) * mm});
            skLineSegment(sketch, "E37.left", {"start": v(66.33, 58.93) * mm, "end": v(66.33, -58.93) * mm});
            skLineSegment(sketch, "E37.right", {"start": v(-66.33, 58.93) * mm, "end": v(-66.33, -58.93) * mm});
            skPoint(sketch, "E37.middle", {"position": v(0, 0) * mm});
            skSolve(sketch);
        }
        {
            var Q0;
            Q0=qCreatedBy(id+"F41.planeOp",FACE);
            var sketch = newSketch(context, id + "F86", { "sketchPlane" : qUnion([Q0])});
            skLineSegment(sketch, "E38.bottom", {"start": v(66.33, 58.93) * mm, "end": v(-66.33, 58.93) * mm});
            skLineSegment(sketch, "E38.top", {"start": v(66.33, -58.93) * mm, "end": v(-66.33, -58.93) * mm});
            skLineSegment(sketch, "E38.left", {"start": v(66.33, 58.93) * mm, "end": v(66.33, -58.93) * mm});
            skLineSegment(sketch, "E38.right", {"start": v(-66.33, 58.93) * mm, "end": v(-66.33, -58.93) * mm});
            skPoint(sketch, "E38.middle", {"position": v(0, 0) * mm});
            skSolve(sketch);
        }
        {
            var Q0;
            Q0=qCreatedBy(id+"F42.planeOp",FACE);
            var sketch = newSketch(context, id + "F87", { "sketchPlane" : qUnion([Q0])});
            skLineSegment(sketch, "E39.bottom", {"start": v(66.92, 59.32) * mm, "end": v(-66.92, 59.32) * mm});
            skLineSegment(sketch, "E39.top", {"start": v(66.92, -59.32) * mm, "end": v(-66.92, -59.32) * mm});
            skLineSegment(sketch, "E39.left", {"start": v(66.92, 59.32) * mm, "end": v(66.92, -59.32) * mm});
            skLineSegment(sketch, "E39.right", {"start": v(-66.92, 59.32) * mm, "end": v(-66.92, -59.32) * mm});
            skPoint(sketch, "E39.middle", {"position": v(0, 0) * mm});
            skSolve(sketch);
        }
        {
            var Q0;
            Q0=qCreatedBy(id+"F43.planeOp",FACE);
            var sketch = newSketch(context, id + "F88", { "sketchPlane" : qUnion([Q0])});
            skLineSegment(sketch, "E40.bottom", {"start": v(66.53, 59.52) * mm, "end": v(-66.53, 59.52) * mm});
            skLineSegment(sketch, "E40.top", {"start": v(66.53, -59.52) * mm, "end": v(-66.53, -59.52) * mm});
            skLineSegment(sketch, "E40.left", {"start": v(66.53, 59.52) * mm, "end": v(66.53, -59.52) * mm});
            skLineSegment(sketch, "E40.right", {"start": v(-66.53, 59.52) * mm, "end": v(-66.53, -59.52) * mm});
            skPoint(sketch, "E40.middle", {"position": v(0, 0) * mm});
            skSolve(sketch);
        }
        {
            var Q0;
            Q0=qCreatedBy(id+"F44.planeOp",FACE);
            var sketch = newSketch(context, id + "F89", { "sketchPlane" : qUnion([Q0])});
            skLineSegment(sketch, "E41.bottom", {"start": v(65.95, 59.13) * mm, "end": v(-65.95, 59.13) * mm});
            skLineSegment(sketch, "E41.top", {"start": v(65.95, -59.13) * mm, "end": v(-65.95, -59.13) * mm});
            skLineSegment(sketch, "E41.left", {"start": v(65.95, 59.13) * mm, "end": v(65.95, -59.13) * mm});
            skLineSegment(sketch, "E41.right", {"start": v(-65.95, 59.13) * mm, "end": v(-65.95, -59.13) * mm});
            skPoint(sketch, "E41.middle", {"position": v(0, 0) * mm});
            skSolve(sketch);
        }
        {
            var Q0;
            Q0 = qSketchRegion(id + "F89", true);
            var Q1;
            Q1 = qSketchRegion(id + "F88", true);
            var Q2;
            Q2 = qSketchRegion(id + "F87", true);
            var Q3;
            Q3 = qSketchRegion(id + "F86", true);
            var Q4;
            Q4 = qSketchRegion(id + "F85", true);
            var Q5;
            Q5 = qSketchRegion(id + "F84", true);
            var Q6;
            Q6 = qSketchRegion(id + "F83", true);
            var Q7;
            Q7 = qSketchRegion(id + "F82", true);
            var Q8;
            Q8 = qSketchRegion(id + "F81", true);
            var Q9;
            Q9 = qSketchRegion(id + "F80", true);
            var Q10;
            Q10 = qSketchRegion(id + "F79", true);
            var Q11;
            Q11 = qSketchRegion(id + "F78", true);
            extrude(context, id + "F90", {"entities" : qUnion([Q0, Q1, Q2, Q3, Q4, Q5, Q6, Q7, Q8, Q9, Q10, Q11]), "operationType" : NewBodyOperationType.REMOVE, "oppositeDirection" : true, "depth" : .4 * mm});
        }
    });
